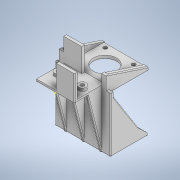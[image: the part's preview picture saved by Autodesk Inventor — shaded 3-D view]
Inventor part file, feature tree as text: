
AUTODESK INVENTOR PART (.ipt)
format: ipt  version: 2020 (Build 240168000, 168)  size: 538,112 bytes
history: native  units: in
note: dims shown in document units (in); Inventor stores cm internally (conversion verified against a paired STEP export)
features: sketch x21, extrude x18, fillet x3, mirror x1, pattern_circular x1
ambient origin geometry x8: Origin, YZ Plane, XZ Plane, XY Plane, X Axis, Y Axis, Z Axis, Center Point
bodies: Solid1 (feature_tree)
feature tree (44):
  extrude  "Extrusion1"  Depth=1.2756in
  extrude  "Extrusion3"  Depth=0.1181in
  extrude  "Extrusion4"  Depth=0.1181in TaperAngle=0.0deg
  extrude  "Extrusion5"  Depth=0.1181in TaperAngle=0.0deg
  extrude  "Extrusion6"  Depth=0.1181in TaperAngle=0.0deg
  extrude  "Extrusion7"  Depth=0.3346in
  extrude  "Extrusion8"  Depth=0.1181in
  sketch  "Sketch14"  dims[d25=0.1575in d26=0.2362in d27=0.0in]
  sketch  "Sketch27"  dims[d28=0.2362in d29=0.2362in]
  extrude  "Extrusion26"  Depth=0.2362in TaperAngle=0.0deg
  extrude  "Extrusion27"  Depth=0.2362in
  sketch  "Sketch30"  dims[d114=2.0079in d115=0.1575in]
  extrude  "Extrusion28"  Depth=0.2953in
  extrude  "Extrusion29"  Depth=0.2953in
  extrude  "Extrusion32"  Depth=0.1575in
  extrude  "Extrusion33"  Depth=0.5512in
  extrude  "Extrusion34"  Depth=0.5512in
  extrude  "Extrusion35"  Depth=0.1181in
  extrude  "Extrusion36"  Depth=0.1181in TaperAngle=0.0deg
  mirror  "Mirror1"
  extrude  "Extrusion37"  Depth=0.1181in
  extrude  "Extrusion38"  Depth=0.1181in
  pattern_circular  "Circular Pattern1"  [2 undecoded]
  fillet  "Fillet3"  Radius=0.1181in
  fillet  "Fillet4"  Radius=0.1181in
  fillet  "Fillet5"  Radius=0.1181in
  sketch  "Sketch1"  dims[d0=1.6142in d1=1.2756in]
  sketch  "Sketch3"  dims[d2=0.1181in d3=0.0in d8=0.1181in]
  sketch  "Sketch4"  dims[d9=0.1181in d10=1.0in d11=0.0in]
  sketch  "Sketch5"  dims[d12=0.8465in d13=0.1181in d14=0.0in]
  sketch  "Sketch6"  dims[d15=0.8465in d16=0.1181in d17=0.0in]
  sketch  "Sketch7"  dims[d20=0.3346in d21=0.3346in]
  sketch  "Sketch8"  dims[d22=0.1181in d23=0.0in d24=0.1575in]
  sketch  "Sketch28"  dims[d30=0.1181in d31=0.0in d54=0.2953in]
  sketch  "Sketch29"  dims[d65=1.0236in d66=0.2953in]
  sketch  "Sketch31"  dims[d116=0.1575in d117=0.5512in]
  sketch  "Sketch32"  dims[d118=0.1575in d119=0.5512in]
  sketch  "Sketch35"  dims[d120=1.6654in d121=0.0in d122=0.1181in]
  sketch  "Sketch36"  dims[d123=0.1181in d124=0.7087in d125=0.0in]
  sketch  "Sketch37"  dims[d126=2.3622in d127=0.1181in]
  sketch  "Sketch38"  dims[d128=0.5906in d129=0.1181in]
  sketch  "Sketch39"  dims[d130=0.5906in]
  sketch  "Sketch40"  dims[d131=0.1181in]
  sketch  "Sketch41"  dims[d132=0.5906in d133=2.2047in d134=0.1575in d135=0.0in d136=0.0in d137=0.1181in d138=0.1181in d139=0.1181in d140=1.4567in d141=0.0in d150=0.9843in d151=0.1575in d152=0.1575in d153=0.1575in d154=0.1575in d155=0.1969in d156=0.0in d157=0.5906in d158=0.1575in d159=0.1575in d160=0.1969in d161=0.0in d162=0.5906in d163=0.1181in d164=0.6693in d165=0.0in d166=0.1575in d167=0.6693in d168=0.0in d169=0.2362in d170=0.3937in d171=0.1181in d172=0.0in d173=2.3622in d174=0.0in d175=0.2362in d176=0.315in d177=0.0787in d178=0.0in d179=1.5748in d180=360.0deg d182=0.0394in d183=0.0394in d184=0.0394in d62=0.0197in d63=0.0344in d64=0.0197in d70=0.0197in d71=0.0344in d72=0.0197in d73=0.0344in]
note: 2 required parameter values undecoded (feature->parameter linkage not recoverable at this tier; creation-order binding heuristic only, values carry confidence <= 0.55)
